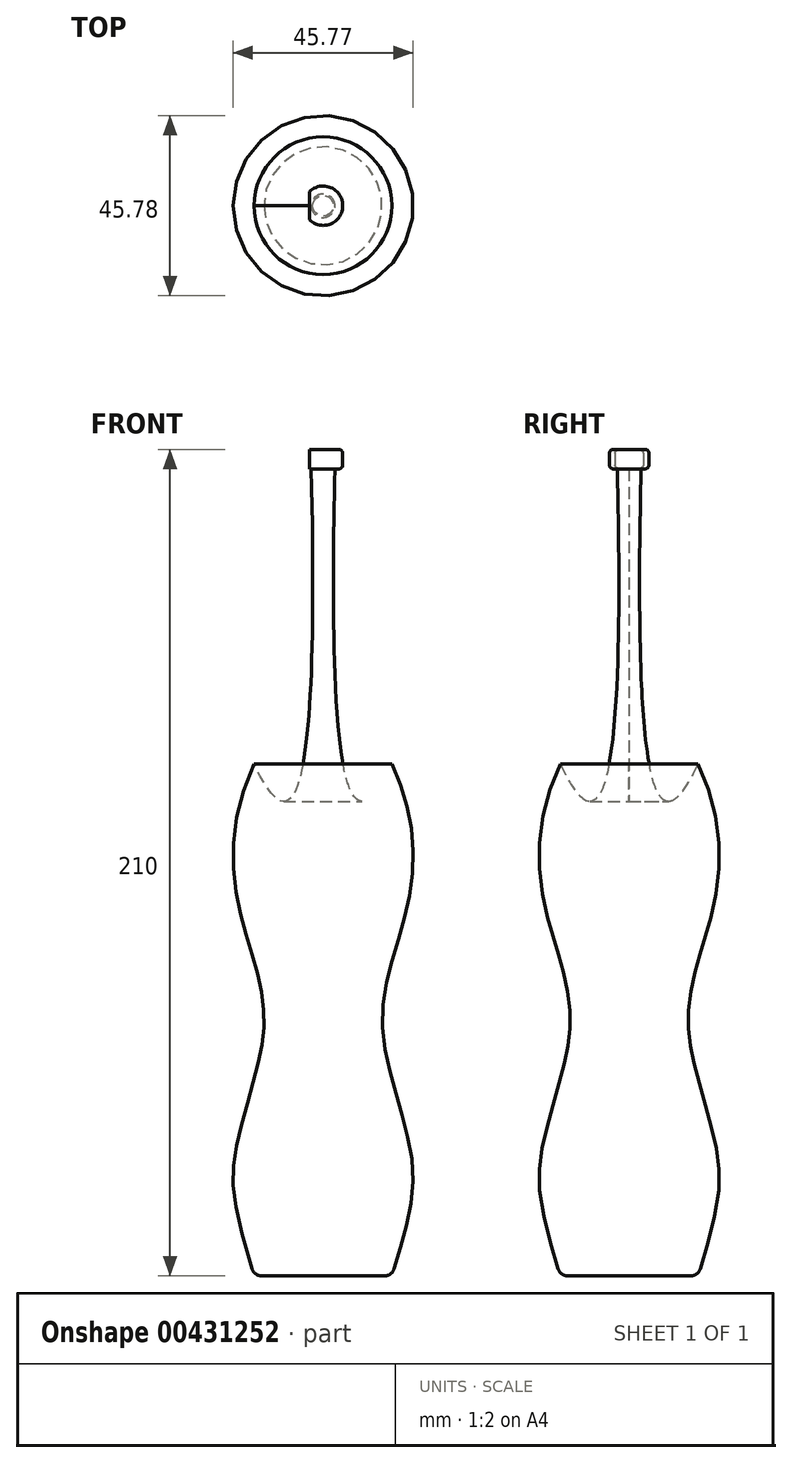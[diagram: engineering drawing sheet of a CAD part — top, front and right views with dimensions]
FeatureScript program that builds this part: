
annotation { "Feature Type Name" : "Feature", "Feature Type Description" : "" }
export const myFeature = defineFeature(function(context is Context, id is Id, definition is map)
    precondition{}
    {
        {
            var Q0;
            Q0=qCreatedBy(makeId("Front.planeOp"),FACE);
            var sketch = newSketch(context, id + "F0", { "sketchPlane" : qUnion([Q0])});
            skLineSegment(sketch, "E0", {"start": v(0, 0) * mm, "end": v(0, 130) * mm});
            skLineSegment(sketch, "E1", {"start": v(17.5, 0) * mm, "end": v(0, 0) * mm});
            skPoint(sketch, "E2", {"position": v(17.5, 80) * mm});
            skPoint(sketch, "E3", {"position": v(17.5, 50) * mm});
            skFitSpline(sketch, "E4", {"points": [v(17.5, 130) * mm, v(22.5, 100) * mm, v(17.5, 80) * mm, v(15, 65) * mm, v(17.5, 50) * mm, v(22.5, 30) * mm, v(17.5, 0) * mm], "startDerivative": vector(75.91, -157) * mm, "endDerivative": vector(-75.91, -246.84) * mm});
            skLineSegment(sketch, "E5", {"start": v(0, 130) * mm, "end": v(0, 205) * mm});
            skLineSegment(sketch, "E6", {"start": v(0, 205) * mm, "end": v(3, 205) * mm});
            skFitSpline(sketch, "E7", {"points": [v(3, 205) * mm, v(17.5, 130) * mm], "startDerivative": vector(-5.35, -225) * mm, "endDerivative": vector(35.77, 75.43) * mm});
            skLineSegment(sketch, "E8.bottom", {"start": v(0, 205) * mm, "end": v(5, 205) * mm});
            skLineSegment(sketch, "E8.top", {"start": v(0, 210) * mm, "end": v(5, 210) * mm});
            skLineSegment(sketch, "E8.left", {"start": v(0, 205) * mm, "end": v(0, 210) * mm});
            skLineSegment(sketch, "E8.right", {"start": v(5, 205) * mm, "end": v(5, 210) * mm});
            skSolve(sketch);
        }
        {
            var Q0;
            Q0=qSketchRegion(id+"F0",true);
            var Q1;
            Q1=sQuery(id+"F0.wireOp",EDGE,"E0");
            revolve(context, id + "F1", {"entities" : qUnion([Q0]), "axis" : qUnion([Q1]), "revolveType" : RevolveType.FULL});
        }
        {
            var Q0;
            Q0=makeQuery(id+"F1.opRevolve","SWEPT_EDGE",EDGE,{"disambiguationData":[OSD([sQuery(id+"F0.wireOp",EDGE,"E1"),sQuery(id+"F0.wireOp",EDGE,"E4")])]});
            fillet(context, id + "F2", {"entities" : qUnion([Q0]), "radius" : 2.54 * mm, "tangentPropagation" : true, "allowEdgeOverflow" : false});
        }
        {
            var Q0;
            Q0=makeQuery(id+"F1.opRevolve","SWEPT_EDGE",EDGE,{"disambiguationData":[OSD([sQuery(id+"F0.wireOp",EDGE,"E8.bottom"),sQuery(id+"F0.wireOp",EDGE,"E8.right")])]});
            var Q1;
            Q1=makeQuery(id+"F1.opRevolve","SWEPT_EDGE",EDGE,{"disambiguationData":[OSD([sQuery(id+"F0.wireOp",EDGE,"E8.top"),sQuery(id+"F0.wireOp",EDGE,"E8.right")])]});
            fillet(context, id + "F3", {"entities" : qUnion([Q0, Q1]), "radius" : 1 * mm, "tangentPropagation" : true, "allowEdgeOverflow" : false});
        }
        {
            var Q0;
            Q0=qCreatedBy(makeId("Front.planeOp"),FACE);
            var sketch = newSketch(context, id + "F4", { "sketchPlane" : qUnion([Q0])});
            skLineSegment(sketch, "E9.bottom", {"start": v(-23.2, 217.63) * mm, "end": v(-3.5, 217.63) * mm});
            skLineSegment(sketch, "E9.top", {"start": v(-23.2, 201.92) * mm, "end": v(-3.5, 201.92) * mm});
            skLineSegment(sketch, "E9.left", {"start": v(-23.2, 217.63) * mm, "end": v(-23.2, 201.92) * mm});
            skLineSegment(sketch, "E9.right", {"start": v(-3.5, 217.63) * mm, "end": v(-3.5, 201.92) * mm});
            skSolve(sketch);
        }
        {
            var Q0;
            Q0=makeQuery(id+"F4.imprint","IMPRINT",FACE,{"disambiguationData":[TD([[makeQuery(id+"F4.imprint","IMPRINT",EDGE,{"derivedFrom":sQuery(id+"F4.wireOp",EDGE,"E9.bottom")}),-1.0]])]});
            extrude(context, id + "F5", {"entities" : qUnion([Q0]), "operationType" : NewBodyOperationType.REMOVE, "endBound" : BoundingType.SYMMETRIC, "depth" : 44.8 * mm});
        }
    });
